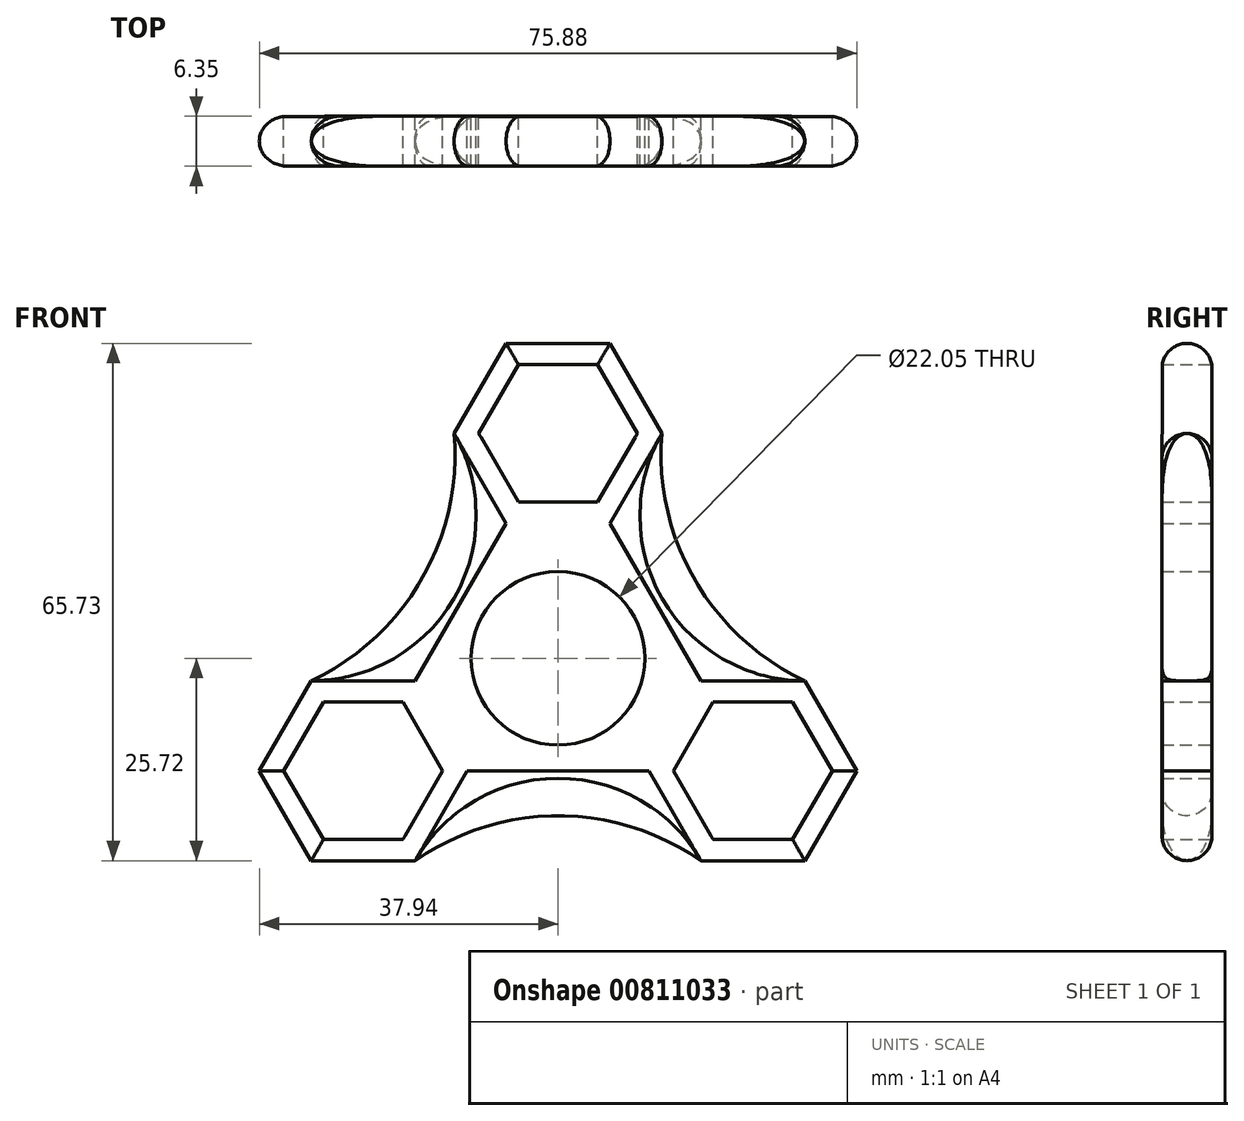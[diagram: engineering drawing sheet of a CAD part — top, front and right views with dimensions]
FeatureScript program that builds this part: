
annotation { "Feature Type Name" : "Feature", "Feature Type Description" : "" }
export const myFeature = defineFeature(function(context is Context, id is Id, definition is map)
    precondition{}
    {
        {
            var Q0;
            Q0=qCreatedBy(makeId("Front.planeOp"),FACE);
            var sketch = newSketch(context, id + "F0", { "sketchPlane" : qUnion([Q0])});
            skCircle(sketch, "E0", {"center": v(0, 0) * mm, "radius": 11.02 * mm});
            skCircle(sketch, "E1", {"center": v(0, 0) * mm, "radius": 14.29 * mm});
            skCircle(sketch, "E2.cCircle", {"center": v(0, 28.58) * mm, "radius": 8.74 * mm, "construction": true});
            skLineSegment(sketch, "E2.0", {"start": v(5.04, 19.84) * mm, "end": v(-5.04, 19.84) * mm});
            skLineSegment(sketch, "E2.1", {"start": v(-5.04, 19.84) * mm, "end": v(-10.09, 28.57) * mm});
            skLineSegment(sketch, "E2.2", {"start": v(-10.09, 28.58) * mm, "end": v(-5.04, 37.31) * mm});
            skLineSegment(sketch, "E2.3", {"start": v(-5.04, 37.31) * mm, "end": v(5.04, 37.31) * mm});
            skLineSegment(sketch, "E2.4", {"start": v(5.04, 37.31) * mm, "end": v(10.09, 28.58) * mm});
            skLineSegment(sketch, "E2.5", {"start": v(10.09, 28.57) * mm, "end": v(5.04, 19.84) * mm});
            skPoint(sketch, "E2.0.midPoint", {"position": v(0, 19.84) * mm});
            skCircle(sketch, "E3.cCircle", {"center": v(0, 28.58) * mm, "radius": 11.43 * mm, "construction": true});
            skLineSegment(sketch, "E3.0", {"start": v(6.6, 17.15) * mm, "end": v(-6.6, 17.15) * mm});
            skLineSegment(sketch, "E3.1", {"start": v(-6.6, 17.15) * mm, "end": v(-13.2, 28.58) * mm});
            skLineSegment(sketch, "E3.2", {"start": v(-13.2, 28.58) * mm, "end": v(-6.6, 40) * mm});
            skLineSegment(sketch, "E3.3", {"start": v(-6.6, 40) * mm, "end": v(6.6, 40) * mm});
            skLineSegment(sketch, "E3.4", {"start": v(6.6, 40) * mm, "end": v(13.2, 28.57) * mm});
            skLineSegment(sketch, "E3.5", {"start": v(13.2, 28.57) * mm, "end": v(6.6, 17.14) * mm});
            skPoint(sketch, "E3.0.midPoint", {"position": v(0, 17.15) * mm});
            skPoint(sketch, "E4.1.0", {"position": v(-14.85, -8.57) * mm});
            skCircle(sketch, "E4.1.1", {"center": v(-24.75, -14.29) * mm, "radius": 8.74 * mm, "construction": true});
            skLineSegment(sketch, "E4.1.2", {"start": v(-19.7, -23.03) * mm, "end": v(-29.8, -23.03) * mm});
            skLineSegment(sketch, "E4.1.3", {"start": v(-31.35, -2.86) * mm, "end": v(-18.15, -2.86) * mm});
            skLineSegment(sketch, "E4.1.4", {"start": v(-37.94, -14.29) * mm, "end": v(-31.35, -2.86) * mm});
            skLineSegment(sketch, "E4.1.5", {"start": v(-31.35, -25.72) * mm, "end": v(-37.94, -14.29) * mm});
            skLineSegment(sketch, "E4.1.6", {"start": v(-29.8, -5.55) * mm, "end": v(-19.7, -5.55) * mm});
            skCircle(sketch, "E4.1.7", {"center": v(-24.75, -14.29) * mm, "radius": 11.43 * mm, "construction": true});
            skLineSegment(sketch, "E4.1.8", {"start": v(-11.55, -14.29) * mm, "end": v(-18.15, -25.72) * mm});
            skLineSegment(sketch, "E4.1.9", {"start": v(-18.15, -25.72) * mm, "end": v(-31.35, -25.72) * mm});
            skPoint(sketch, "E4.1.10", {"position": v(-17.18, -9.92) * mm});
            skLineSegment(sketch, "E4.1.11", {"start": v(-19.7, -5.55) * mm, "end": v(-14.66, -14.29) * mm});
            skLineSegment(sketch, "E4.1.12", {"start": v(-14.66, -14.29) * mm, "end": v(-19.7, -23.03) * mm});
            skLineSegment(sketch, "E4.1.13", {"start": v(-29.8, -23.03) * mm, "end": v(-34.84, -14.29) * mm});
            skLineSegment(sketch, "E4.1.14", {"start": v(-34.84, -14.29) * mm, "end": v(-29.8, -5.55) * mm});
            skLineSegment(sketch, "E4.1.15", {"start": v(-18.15, -2.86) * mm, "end": v(-11.55, -14.29) * mm});
            skPoint(sketch, "E4.2.0", {"position": v(14.85, -8.57) * mm});
            skCircle(sketch, "E4.2.1", {"center": v(24.75, -14.29) * mm, "radius": 8.74 * mm, "construction": true});
            skLineSegment(sketch, "E4.2.2", {"start": v(29.8, -5.55) * mm, "end": v(34.84, -14.29) * mm});
            skLineSegment(sketch, "E4.2.3", {"start": v(18.15, -25.72) * mm, "end": v(11.55, -14.29) * mm});
            skLineSegment(sketch, "E4.2.4", {"start": v(31.35, -25.72) * mm, "end": v(18.15, -25.72) * mm});
            skLineSegment(sketch, "E4.2.5", {"start": v(37.94, -14.29) * mm, "end": v(31.35, -25.72) * mm});
            skLineSegment(sketch, "E4.2.6", {"start": v(19.7, -23.03) * mm, "end": v(14.66, -14.29) * mm});
            skCircle(sketch, "E4.2.7", {"center": v(24.75, -14.29) * mm, "radius": 11.43 * mm, "construction": true});
            skLineSegment(sketch, "E4.2.8", {"start": v(18.15, -2.86) * mm, "end": v(31.35, -2.86) * mm});
            skLineSegment(sketch, "E4.2.9", {"start": v(31.35, -2.86) * mm, "end": v(37.94, -14.29) * mm});
            skPoint(sketch, "E4.2.10", {"position": v(17.18, -9.92) * mm});
            skLineSegment(sketch, "E4.2.11", {"start": v(14.66, -14.29) * mm, "end": v(19.7, -5.55) * mm});
            skLineSegment(sketch, "E4.2.12", {"start": v(19.7, -5.55) * mm, "end": v(29.8, -5.55) * mm});
            skLineSegment(sketch, "E4.2.13", {"start": v(34.84, -14.29) * mm, "end": v(29.8, -23.03) * mm});
            skLineSegment(sketch, "E4.2.14", {"start": v(29.8, -23.03) * mm, "end": v(19.7, -23.03) * mm});
            skLineSegment(sketch, "E4.2.15", {"start": v(11.55, -14.29) * mm, "end": v(18.15, -2.86) * mm});
            skLineSegment(sketch, "E5", {"start": v(-11.55, -14.29) * mm, "end": v(11.55, -14.29) * mm});
            skLineSegment(sketch, "E6", {"start": v(18.15, -2.86) * mm, "end": v(6.6, 17.15) * mm});
            skLineSegment(sketch, "E7", {"start": v(-6.6, 17.15) * mm, "end": v(-18.15, -2.86) * mm});
            skArc(sketch, "E8", {"start": v(-31.35, -2.86) * mm, "mid": v(-13.2, 7.62) * mm, "end": v(-13.2, 28.58) * mm});
            skArc(sketch, "E9", {"start": v(-31.35, -2.86) * mm, "mid": v(-17.34, 10) * mm, "end": v(-13.2, 28.58) * mm});
            skArc(sketch, "E10", {"start": v(13.2, 28.57) * mm, "mid": v(13.2, 7.62) * mm, "end": v(31.35, -2.86) * mm});
            skArc(sketch, "E11", {"start": v(13.2, 28.57) * mm, "mid": v(17.34, 10) * mm, "end": v(31.35, -2.86) * mm});
            skArc(sketch, "E12", {"start": v(18.15, -25.72) * mm, "mid": v(0, -15.24) * mm, "end": v(-18.15, -25.72) * mm});
            skArc(sketch, "E13", {"start": v(18.15, -25.72) * mm, "mid": v(0, -20.02) * mm, "end": v(-18.15, -25.72) * mm});
            skSolve(sketch);
        }
        {
            var Q0;
            Q0=makeQuery(id+"F0.imprint","IMPRINT",FACE,{"disambiguationData":[TD([[makeQuery(id+"F0.imprint","IMPRINT",EDGE,{"derivedFrom":sQuery(id+"F0.wireOp",EDGE,"E8")}),1.0]])]});
            var Q1;
            Q1=makeQuery(id+"F0.imprint","IMPRINT",FACE,{"disambiguationData":[TD([[makeQuery(id+"F0.imprint","IMPRINT",EDGE,{"derivedFrom":sQuery(id+"F0.wireOp",EDGE,"E10")}),1.0]])]});
            var Q2;
            Q2=makeQuery(id+"F0.imprint","IMPRINT",FACE,{"disambiguationData":[TD([[makeQuery(id+"F0.imprint","IMPRINT",EDGE,{"derivedFrom":sQuery(id+"F0.wireOp",EDGE,"E12")}),1.0]])]});
            var Q3;
            Q3=makeQuery(id+"F0.imprint","IMPRINT",FACE,{"disambiguationData":[TD([[makeQuery(id+"F0.imprint","IMPRINT",EDGE,{"derivedFrom":sQuery(id+"F0.wireOp",EDGE,"E2.0")}),1.0]])]});
            var Q4;
            Q4=makeQuery(id+"F0.imprint","IMPRINT",FACE,{"disambiguationData":[TD([[makeQuery(id+"F0.imprint","IMPRINT",EDGE,{"derivedFrom":sQuery(id+"F0.wireOp",EDGE,"E4.1.2")}),1.0]])]});
            var Q5;
            Q5=makeQuery(id+"F0.imprint","IMPRINT",FACE,{"disambiguationData":[TD([[makeQuery(id+"F0.imprint","IMPRINT",EDGE,{"derivedFrom":sQuery(id+"F0.wireOp",EDGE,"E4.2.2")}),1.0]])]});
            var Q6;
            Q6=makeQuery(id+"F0.imprint","IMPRINT",FACE,{"disambiguationData":[TD([[makeQuery(id+"F0.imprint","IMPRINT",EDGE,{"derivedFrom":sQuery(id+"F0.wireOp",EDGE,"E0")}),-1.0]])]});
            var Q7;
            {var subQ5=sQuery(id+"F0.wireOp",EDGE,"E4.2.15");Q7=makeQuery(id+"F0.imprint","IMPRINT",FACE,{"disambiguationData":[TD([[makeQuery(id+"F0.imprint","IMPRINT",EDGE,{"derivedFrom":subQ5}),1.0]])]});}
            var Q8;
            {var subQ5=sQuery(id+"F0.wireOp",EDGE,"E4.1.15");Q8=makeQuery(id+"F0.imprint","IMPRINT",FACE,{"disambiguationData":[TD([[makeQuery(id+"F0.imprint","IMPRINT",EDGE,{"derivedFrom":subQ5}),1.0]])]});}
            var Q9;
            {var subQ5=sQuery(id+"F0.wireOp",EDGE,"E3.0");Q9=makeQuery(id+"F0.imprint","IMPRINT",FACE,{"disambiguationData":[TD([[makeQuery(id+"F0.imprint","IMPRINT",EDGE,{"derivedFrom":subQ5}),1.0]])]});}
            extrude(context, id + "F1", {"entities" : qUnion([Q0, Q1, Q2, Q3, Q4, Q5, Q6, Q7, Q8, Q9]), "depth" : 6.35 * mm, "offsetDistance" : 25.4 * mm});
        }
        {
            var Q0;
            Q0=makeQuery(id+"F1.opExtrude","CAP_EDGE",EDGE,{"disambiguationData":[OSD([sQuery(id+"F0.wireOp",EDGE,"E3.2")])],"isStart":false});
            var Q1;
            Q1=makeQuery(id+"F1.opExtrude","CAP_EDGE",EDGE,{"disambiguationData":[OSD([sQuery(id+"F0.wireOp",EDGE,"E3.3")])],"isStart":false});
            var Q2;
            Q2=makeQuery(id+"F1.opExtrude","CAP_EDGE",EDGE,{"disambiguationData":[OSD([sQuery(id+"F0.wireOp",EDGE,"E3.4")])],"isStart":false});
            var Q3;
            Q3=makeQuery(id+"F1.opExtrude","CAP_EDGE",EDGE,{"disambiguationData":[OSD([sQuery(id+"F0.wireOp",EDGE,"E9")])],"isStart":false});
            var Q4;
            Q4=makeQuery(id+"F1.opExtrude","CAP_EDGE",EDGE,{"disambiguationData":[OSD([sQuery(id+"F0.wireOp",EDGE,"E4.1.4")])],"isStart":false});
            var Q5;
            Q5=makeQuery(id+"F1.opExtrude","CAP_EDGE",EDGE,{"disambiguationData":[OSD([sQuery(id+"F0.wireOp",EDGE,"E4.1.5")])],"isStart":false});
            var Q6;
            Q6=makeQuery(id+"F1.opExtrude","CAP_EDGE",EDGE,{"disambiguationData":[OSD([sQuery(id+"F0.wireOp",EDGE,"E4.1.9")])],"isStart":false});
            var Q7;
            Q7=makeQuery(id+"F1.opExtrude","CAP_EDGE",EDGE,{"disambiguationData":[OSD([sQuery(id+"F0.wireOp",EDGE,"E13")])],"isStart":false});
            var Q8;
            Q8=makeQuery(id+"F1.opExtrude","CAP_EDGE",EDGE,{"disambiguationData":[OSD([sQuery(id+"F0.wireOp",EDGE,"E4.2.4")])],"isStart":false});
            var Q9;
            Q9=makeQuery(id+"F1.opExtrude","CAP_EDGE",EDGE,{"disambiguationData":[OSD([sQuery(id+"F0.wireOp",EDGE,"E4.2.5")])],"isStart":false});
            var Q10;
            Q10=makeQuery(id+"F1.opExtrude","CAP_EDGE",EDGE,{"disambiguationData":[OSD([sQuery(id+"F0.wireOp",EDGE,"E4.2.9")])],"isStart":false});
            var Q11;
            Q11=makeQuery(id+"F1.opExtrude","CAP_EDGE",EDGE,{"disambiguationData":[OSD([sQuery(id+"F0.wireOp",EDGE,"E11")])],"isStart":false});
            fillet(context, id + "F2", {"entities" : qUnion([Q0, Q1, Q2, Q3, Q4, Q5, Q6, Q7, Q8, Q9, Q10, Q11]), "radius" : 3.17 * mm, "tangentPropagation" : true, "allowEdgeOverflow" : false});
        }
        {
            var Q0;
            Q0=makeQuery(id+"F1.opExtrude","CAP_EDGE",EDGE,{"disambiguationData":[OSD([sQuery(id+"F0.wireOp",EDGE,"E3.3")])],"isStart":true});
            var Q1;
            Q1=makeQuery(id+"F1.opExtrude","CAP_EDGE",EDGE,{"disambiguationData":[OSD([sQuery(id+"F0.wireOp",EDGE,"E3.4")])],"isStart":true});
            var Q2;
            Q2=makeQuery(id+"F1.opExtrude","CAP_EDGE",EDGE,{"disambiguationData":[OSD([sQuery(id+"F0.wireOp",EDGE,"E11")])],"isStart":true});
            var Q3;
            Q3=makeQuery(id+"F1.opExtrude","CAP_EDGE",EDGE,{"disambiguationData":[OSD([sQuery(id+"F0.wireOp",EDGE,"E4.2.9")])],"isStart":true});
            var Q4;
            Q4=makeQuery(id+"F1.opExtrude","CAP_EDGE",EDGE,{"disambiguationData":[OSD([sQuery(id+"F0.wireOp",EDGE,"E4.2.5")])],"isStart":true});
            var Q5;
            Q5=makeQuery(id+"F1.opExtrude","CAP_EDGE",EDGE,{"disambiguationData":[OSD([sQuery(id+"F0.wireOp",EDGE,"E4.2.4")])],"isStart":true});
            var Q6;
            Q6=makeQuery(id+"F1.opExtrude","CAP_EDGE",EDGE,{"disambiguationData":[OSD([sQuery(id+"F0.wireOp",EDGE,"E13")])],"isStart":true});
            var Q7;
            Q7=makeQuery(id+"F1.opExtrude","CAP_EDGE",EDGE,{"disambiguationData":[OSD([sQuery(id+"F0.wireOp",EDGE,"E4.1.9")])],"isStart":true});
            var Q8;
            Q8=makeQuery(id+"F1.opExtrude","CAP_EDGE",EDGE,{"disambiguationData":[OSD([sQuery(id+"F0.wireOp",EDGE,"E4.1.5")])],"isStart":true});
            var Q9;
            Q9=makeQuery(id+"F1.opExtrude","CAP_EDGE",EDGE,{"disambiguationData":[OSD([sQuery(id+"F0.wireOp",EDGE,"E4.1.4")])],"isStart":true});
            var Q10;
            Q10=makeQuery(id+"F1.opExtrude","CAP_EDGE",EDGE,{"disambiguationData":[OSD([sQuery(id+"F0.wireOp",EDGE,"E9")])],"isStart":true});
            var Q11;
            Q11=makeQuery(id+"F1.opExtrude","CAP_EDGE",EDGE,{"disambiguationData":[OSD([sQuery(id+"F0.wireOp",EDGE,"E3.2")])],"isStart":true});
            fillet(context, id + "F3", {"entities" : qUnion([Q0, Q1, Q2, Q3, Q4, Q5, Q6, Q7, Q8, Q9, Q10, Q11]), "radius" : 3.17 * mm, "tangentPropagation" : true, "allowEdgeOverflow" : false});
        }
    });
